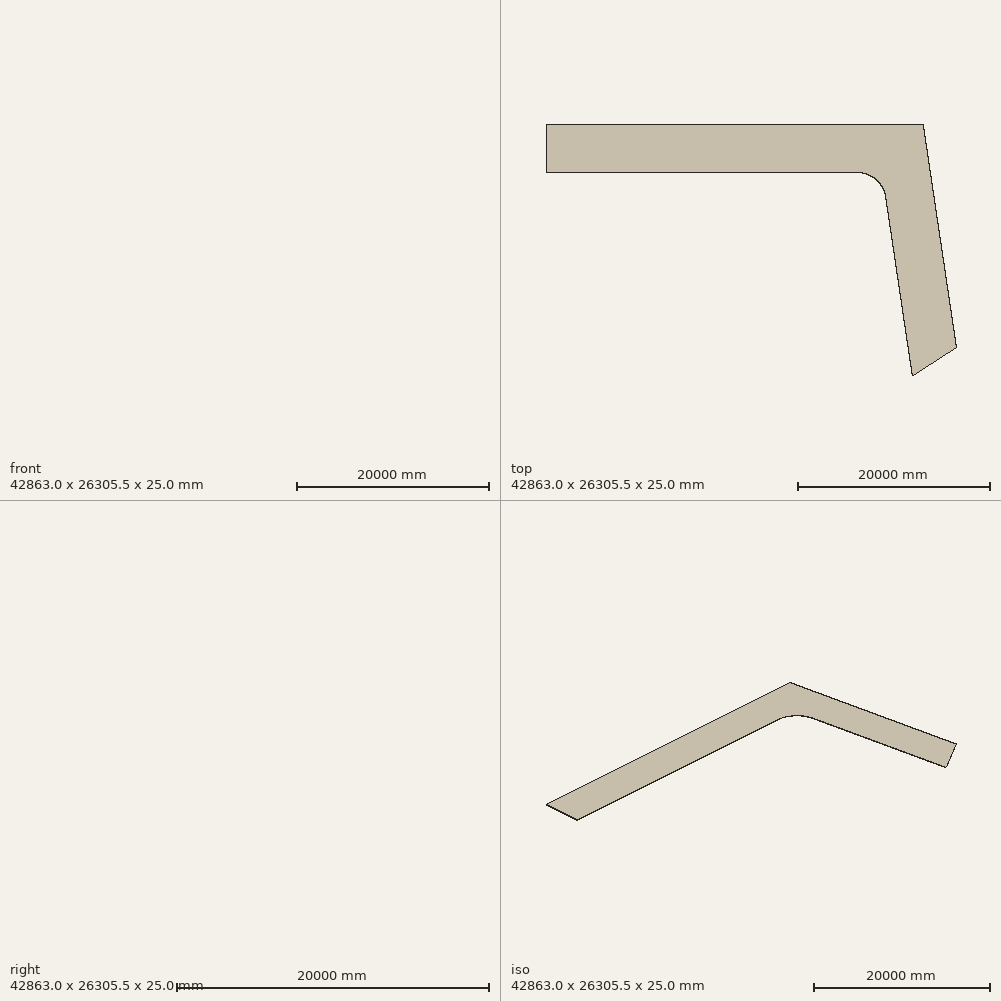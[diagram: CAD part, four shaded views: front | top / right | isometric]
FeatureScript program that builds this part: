
annotation { "Feature Type Name" : "Feature", "Feature Type Description" : "" }
export const myFeature = defineFeature(function(context is Context, id is Id, definition is map)
    precondition{}
    {
        {
            var Q0;
            Q0=qCreatedBy(makeId("Top.planeOp"),FACE);
            var sketch = newSketch(context, id + "F0", { "sketchPlane" : qUnion([Q0])});
            skLineSegment(sketch, "E0", {"start": v(-19746.52, 2463.27) * mm, "end": v(-24982.84, 2463.27) * mm});
            skLineSegment(sketch, "E1", {"start": v(15138.48, 2519.13) * mm, "end": v(17880.13, -15859.75) * mm});
            skLineSegment(sketch, "E2.0", {"start": v(10472.98, -94.1) * mm, "end": v(13269.7, -18842.19) * mm});
            skLineSegment(sketch, "E3", {"start": v(-19746.52, 2463.27) * mm, "end": v(7505.8, 2463.27) * mm});
            skPoint(sketch, "E4.visualSharp", {"position": v(10091.48, 2463.27) * mm});
            skArc(sketch, "E4.filletArc", {"start": v(10472.98, -94.1) * mm, "mid": v(9464.4, 1735.7) * mm, "end": v(7505.8, 2463.27) * mm});
            skLineSegment(sketch, "E5.0", {"start": v(-19746.52, 7463.27) * mm, "end": v(-24982.84, 7463.27) * mm});
            skLineSegment(sketch, "E5.1", {"start": v(-19746.52, 7463.27) * mm, "end": v(14400.94, 7463.27) * mm});
            skLineSegment(sketch, "E6", {"start": v(15138.48, 2519.13) * mm, "end": v(14400.94, 7463.27) * mm});
            skLineSegment(sketch, "E7", {"start": v(-24982.84, 2463.27) * mm, "end": v(-24982.84, 7463.27) * mm});
            skLineSegment(sketch, "E8", {"start": v(13269.7, -18842.19) * mm, "end": v(17880.13, -15859.75) * mm});
            skSolve(sketch);
        }
        {
            var Q0;
            Q0 = qSketchRegion(id + "F0", true);
            extrude(context, id + "F1", {"entities" : qUnion([Q0]), "depth" : 25 * mm});
        }
    });
